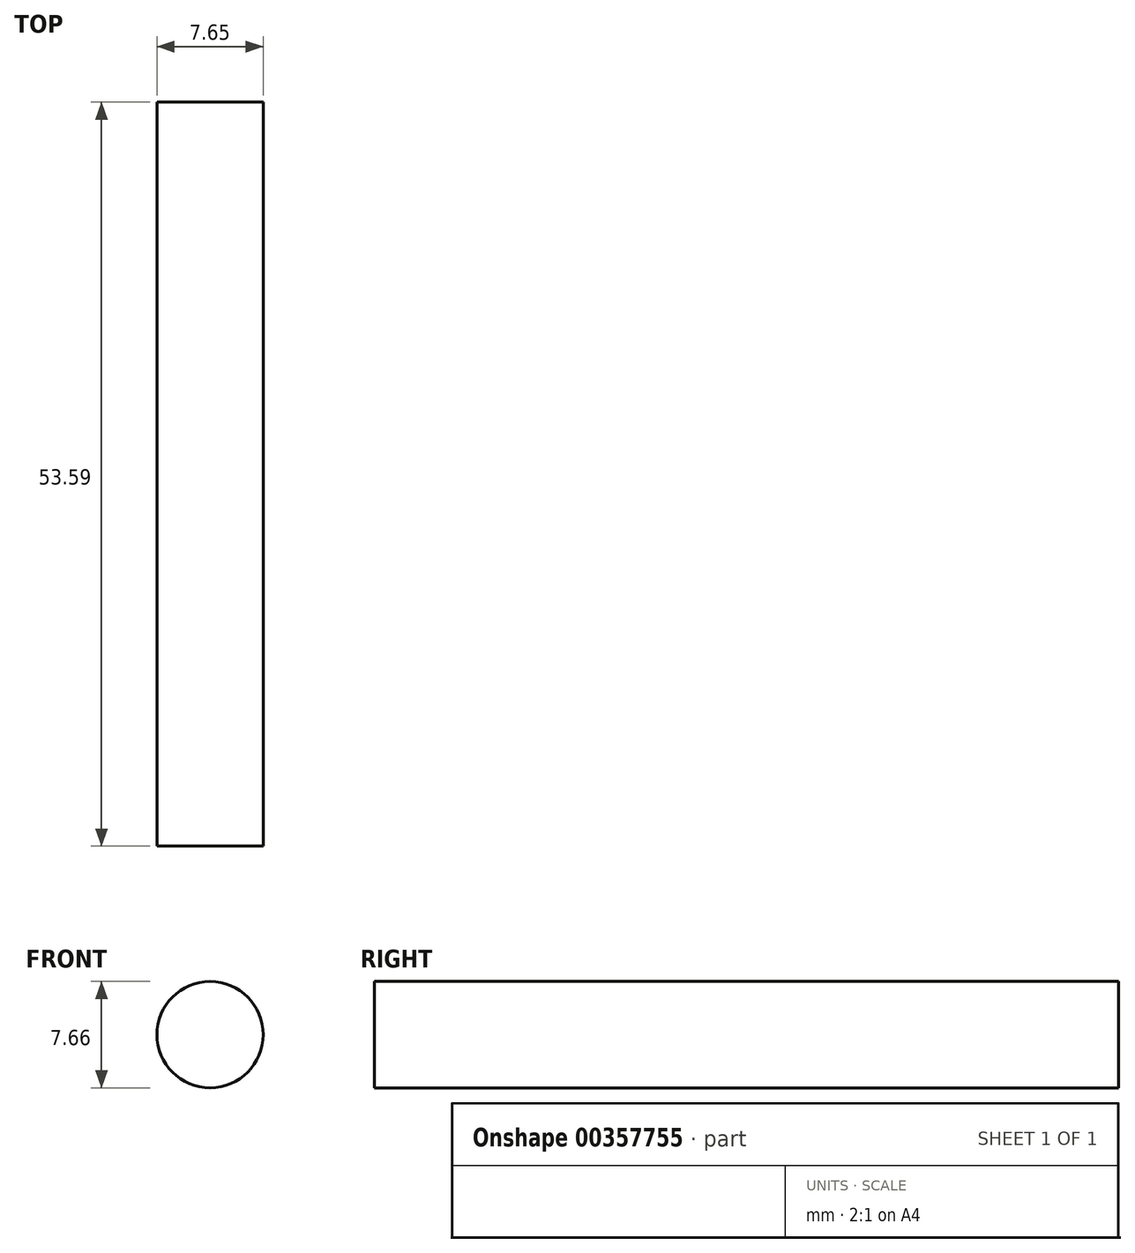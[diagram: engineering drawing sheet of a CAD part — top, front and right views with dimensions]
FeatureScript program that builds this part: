
annotation { "Feature Type Name" : "Feature", "Feature Type Description" : "" }
export const myFeature = defineFeature(function(context is Context, id is Id, definition is map)
    precondition{}
    {
        {
            var Q0;
            Q0=qCreatedBy(makeId("Top.planeOp"),FACE);
            var sketch = newSketch(context, id + "F0", { "sketchPlane" : qUnion([Q0])});
            skLineSegment(sketch, "E0", {"start": v(33.94, -23.86) * mm, "end": v(33.94, 29.73) * mm});
            skLineSegment(sketch, "E1", {"start": v(33.94, 29.73) * mm, "end": v(30.12, 29.73) * mm});
            skLineSegment(sketch, "E2", {"start": v(30.12, 29.73) * mm, "end": v(30.12, -23.86) * mm});
            skLineSegment(sketch, "E3", {"start": v(30.12, -23.86) * mm, "end": v(33.94, -23.86) * mm});
            skSolve(sketch);
        }
        {
            var Q0;
            Q0=makeQuery(id+"F0.imprint","IMPRINT",FACE,{"disambiguationData":[TD([[makeQuery(id+"F0.imprint","IMPRINT",EDGE,{"derivedFrom":sQuery(id+"F0.wireOp",EDGE,"E0")}),1.0]])]});
            var Q1;
            Q1=sQuery(id+"F0.wireOp",EDGE,"E2");
            revolve(context, id + "F1", {"entities" : qUnion([Q0]), "axis" : qUnion([Q1]), "revolveType" : RevolveType.FULL});
        }
    });
